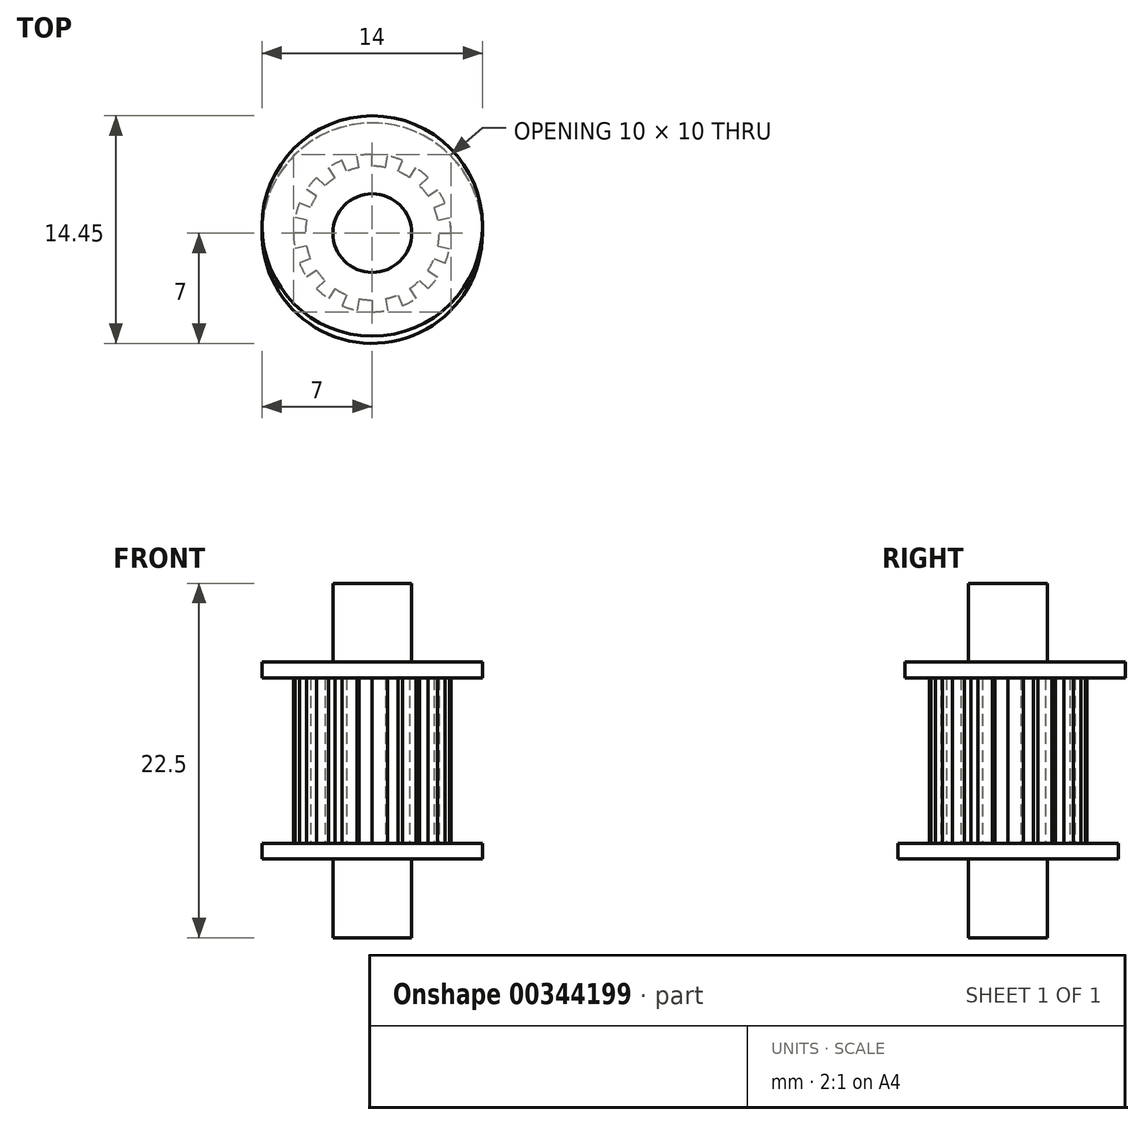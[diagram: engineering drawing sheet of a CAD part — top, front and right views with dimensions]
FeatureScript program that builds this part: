
annotation { "Feature Type Name" : "Feature", "Feature Type Description" : "" }
export const myFeature = defineFeature(function(context is Context, id is Id, definition is map)
    precondition{}
    {
        {
            var Q0;
            Q0=qCreatedBy(makeId("Top.planeOp"),FACE);
            var sketch = newSketch(context, id + "F0", { "sketchPlane" : qUnion([Q0])});
            skCircle(sketch, "E0", {"center": v(0, 0) * mm, "radius": 7 * mm});
            skSolve(sketch);
        }
        {
            var Q0;
            Q0=qSketchRegion(id+"F0",true);
            extrude(context, id + "F1", {"entities" : qUnion([Q0]), "depth" : 1 * mm});
        }
        {
            var Q0;
            Q0=makeQuery(id+"F1.opExtrude","CAP_FACE",FACE,{"disambiguationData":[OSD([sQuery(id+"F0.wireOp",EDGE,"E0")])],"isStart":false});
            var sketch = newSketch(context, id + "F2", { "sketchPlane" : qUnion([Q0])});
            skLineSegment(sketch, "E1", {"start": v(0, 4.25) * mm, "end": v(0, 5) * mm});
            skLineSegment(sketch, "E2.1.0", {"start": v(-0.83, 4.17) * mm, "end": v(-0.98, 4.9) * mm});
            skLineSegment(sketch, "E2.2.0", {"start": v(-1.63, 3.93) * mm, "end": v(-1.91, 4.62) * mm});
            skLineSegment(sketch, "E2.3.0", {"start": v(-2.36, 3.53) * mm, "end": v(-2.78, 4.16) * mm});
            skLineSegment(sketch, "E2.4.0", {"start": v(-3, 3) * mm, "end": v(-3.54, 3.54) * mm});
            skLineSegment(sketch, "E2.5.0", {"start": v(-3.53, 2.36) * mm, "end": v(-4.16, 2.78) * mm});
            skLineSegment(sketch, "E2.6.0", {"start": v(-3.93, 1.63) * mm, "end": v(-4.62, 1.91) * mm});
            skLineSegment(sketch, "E2.7.0", {"start": v(-4.17, 0.83) * mm, "end": v(-4.9, 0.98) * mm});
            skLineSegment(sketch, "E2.8.0", {"start": v(-4.25, 0) * mm, "end": v(-5, 0) * mm});
            skLineSegment(sketch, "E2.9.0", {"start": v(-4.17, -0.83) * mm, "end": v(-4.9, -0.98) * mm});
            skLineSegment(sketch, "E2.10.0", {"start": v(-3.93, -1.63) * mm, "end": v(-4.62, -1.91) * mm});
            skLineSegment(sketch, "E2.11.0", {"start": v(-3.53, -2.36) * mm, "end": v(-4.16, -2.78) * mm});
            skLineSegment(sketch, "E2.12.0", {"start": v(-3, -3) * mm, "end": v(-3.54, -3.54) * mm});
            skLineSegment(sketch, "E2.13.0", {"start": v(-2.36, -3.53) * mm, "end": v(-2.78, -4.16) * mm});
            skLineSegment(sketch, "E2.14.0", {"start": v(-1.63, -3.93) * mm, "end": v(-1.91, -4.62) * mm});
            skLineSegment(sketch, "E2.15.0", {"start": v(-0.83, -4.17) * mm, "end": v(-0.98, -4.9) * mm});
            skLineSegment(sketch, "E2.16.0", {"start": v(0, -4.25) * mm, "end": v(0, -5) * mm});
            skLineSegment(sketch, "E2.17.0", {"start": v(0.83, -4.17) * mm, "end": v(0.98, -4.9) * mm});
            skLineSegment(sketch, "E2.18.0", {"start": v(1.63, -3.93) * mm, "end": v(1.91, -4.62) * mm});
            skLineSegment(sketch, "E2.19.0", {"start": v(2.36, -3.53) * mm, "end": v(2.78, -4.16) * mm});
            skLineSegment(sketch, "E2.20.0", {"start": v(3, -3) * mm, "end": v(3.54, -3.54) * mm});
            skLineSegment(sketch, "E2.21.0", {"start": v(3.53, -2.36) * mm, "end": v(4.16, -2.78) * mm});
            skLineSegment(sketch, "E2.22.0", {"start": v(3.93, -1.63) * mm, "end": v(4.62, -1.91) * mm});
            skLineSegment(sketch, "E2.23.0", {"start": v(4.17, -0.83) * mm, "end": v(4.9, -0.98) * mm});
            skLineSegment(sketch, "E2.24.0", {"start": v(4.25, 0) * mm, "end": v(5, 0) * mm});
            skLineSegment(sketch, "E2.25.0", {"start": v(4.17, 0.83) * mm, "end": v(4.9, 0.98) * mm});
            skLineSegment(sketch, "E2.26.0", {"start": v(3.93, 1.63) * mm, "end": v(4.62, 1.91) * mm});
            skLineSegment(sketch, "E2.27.0", {"start": v(3.53, 2.36) * mm, "end": v(4.16, 2.78) * mm});
            skLineSegment(sketch, "E2.28.0", {"start": v(3, 3) * mm, "end": v(3.54, 3.54) * mm});
            skLineSegment(sketch, "E2.29.0", {"start": v(2.36, 3.53) * mm, "end": v(2.78, 4.16) * mm});
            skLineSegment(sketch, "E2.30.0", {"start": v(1.63, 3.93) * mm, "end": v(1.91, 4.62) * mm});
            skLineSegment(sketch, "E2.31.0", {"start": v(0.83, 4.17) * mm, "end": v(0.98, 4.9) * mm});
            skPoint(sketch, "E2.center", {"position": v(0, 0) * mm});
            skArc(sketch, "E3", {"start": v(-0.83, 4.17) * mm, "mid": v(-1.23, 4.07) * mm, "end": v(-1.63, 3.93) * mm});
            skArc(sketch, "E4", {"start": v(-1.91, 4.62) * mm, "mid": v(-2.36, 4.4) * mm, "end": v(-2.78, 4.16) * mm});
            skPoint(sketch, "E5.orphan", {"position": v(-1.14, 5.75) * mm});
            skArc(sketch, "E6.trimOffspring", {"start": v(0, 5) * mm, "mid": v(-0.5, 4.98) * mm, "end": v(-0.98, 4.9) * mm});
            skArc(sketch, "E7.trimOffspring", {"start": v(0.83, 4.17) * mm, "mid": v(0.42, 4.23) * mm, "end": v(0, 4.25) * mm});
            skArc(sketch, "E8.trimOffspring", {"start": v(1.91, 4.62) * mm, "mid": v(1.45, 4.78) * mm, "end": v(0.98, 4.9) * mm});
            skArc(sketch, "E9.trimOffspring", {"start": v(2.36, 3.53) * mm, "mid": v(2, 3.75) * mm, "end": v(1.63, 3.93) * mm});
            skArc(sketch, "E10.trimOffspring", {"start": v(3.54, 3.54) * mm, "mid": v(3.17, 3.87) * mm, "end": v(2.78, 4.16) * mm});
            skArc(sketch, "E11.trimOffspring", {"start": v(3.53, 2.36) * mm, "mid": v(3.29, 2.7) * mm, "end": v(3, 3) * mm});
            skArc(sketch, "E12.trimOffspring", {"start": v(4.62, 1.91) * mm, "mid": v(4.4, 2.36) * mm, "end": v(4.16, 2.78) * mm});
            skArc(sketch, "E13.trimOffspring", {"start": v(4.17, 0.83) * mm, "mid": v(4.07, 1.23) * mm, "end": v(3.93, 1.63) * mm});
            skArc(sketch, "E14.trimOffspring", {"start": v(5, 0) * mm, "mid": v(4.98, 0.5) * mm, "end": v(4.9, 0.98) * mm});
            skArc(sketch, "E15.trimOffspring", {"start": v(4.17, -0.83) * mm, "mid": v(4.23, -0.42) * mm, "end": v(4.25, 0) * mm});
            skArc(sketch, "E16.trimOffspring", {"start": v(4.62, -1.91) * mm, "mid": v(4.78, -1.45) * mm, "end": v(4.9, -0.98) * mm});
            skArc(sketch, "E17.trimOffspring", {"start": v(3.53, -2.36) * mm, "mid": v(3.75, -2) * mm, "end": v(3.93, -1.63) * mm});
            skArc(sketch, "E18.trimOffspring", {"start": v(3.54, -3.54) * mm, "mid": v(3.87, -3.17) * mm, "end": v(4.16, -2.78) * mm});
            skArc(sketch, "E19.trimOffspring", {"start": v(2.36, -3.53) * mm, "mid": v(2.7, -3.29) * mm, "end": v(3, -3) * mm});
            skArc(sketch, "E20.trimOffspring", {"start": v(1.91, -4.62) * mm, "mid": v(2.36, -4.4) * mm, "end": v(2.78, -4.16) * mm});
            skArc(sketch, "E21.trimOffspring", {"start": v(0.83, -4.17) * mm, "mid": v(1.23, -4.07) * mm, "end": v(1.63, -3.93) * mm});
            skArc(sketch, "E22.trimOffspring", {"start": v(0, -5) * mm, "mid": v(0.5, -4.98) * mm, "end": v(0.98, -4.9) * mm});
            skArc(sketch, "E23.trimOffspring", {"start": v(-0.83, -4.17) * mm, "mid": v(-0.42, -4.23) * mm, "end": v(0, -4.25) * mm});
            skArc(sketch, "E24.trimOffspring", {"start": v(-2.36, -3.53) * mm, "mid": v(-2, -3.75) * mm, "end": v(-1.63, -3.93) * mm});
            skArc(sketch, "E25.trimOffspring", {"start": v(-3.53, -2.36) * mm, "mid": v(-3.29, -2.7) * mm, "end": v(-3, -3) * mm});
            skArc(sketch, "E26.trimOffspring", {"start": v(-4.17, -0.83) * mm, "mid": v(-4.07, -1.23) * mm, "end": v(-3.93, -1.63) * mm});
            skArc(sketch, "E27.trimOffspring", {"start": v(-4.17, 0.83) * mm, "mid": v(-4.23, 0.42) * mm, "end": v(-4.25, 0) * mm});
            skArc(sketch, "E28.trimOffspring", {"start": v(-3.53, 2.36) * mm, "mid": v(-3.75, 2) * mm, "end": v(-3.93, 1.63) * mm});
            skArc(sketch, "E29.trimOffspring", {"start": v(-2.36, 3.53) * mm, "mid": v(-2.7, 3.29) * mm, "end": v(-3, 3) * mm});
            skArc(sketch, "E30.trimOffspring", {"start": v(-3.54, 3.54) * mm, "mid": v(-3.87, 3.17) * mm, "end": v(-4.16, 2.78) * mm});
            skArc(sketch, "E31.trimOffspring", {"start": v(-4.62, 1.91) * mm, "mid": v(-4.78, 1.45) * mm, "end": v(-4.9, 0.98) * mm});
            skArc(sketch, "E32.trimOffspring", {"start": v(-5, 0) * mm, "mid": v(-4.98, -0.5) * mm, "end": v(-4.9, -0.98) * mm});
            skArc(sketch, "E33.trimOffspring", {"start": v(-4.62, -1.91) * mm, "mid": v(-4.4, -2.36) * mm, "end": v(-4.16, -2.78) * mm});
            skArc(sketch, "E34.trimOffspring", {"start": v(-3.54, -3.54) * mm, "mid": v(-3.17, -3.87) * mm, "end": v(-2.78, -4.16) * mm});
            skArc(sketch, "E35.trimOffspring", {"start": v(-1.91, -4.62) * mm, "mid": v(-1.45, -4.78) * mm, "end": v(-0.98, -4.9) * mm});
            skPoint(sketch, "E36.orphan", {"position": v(1.14, 5.75) * mm});
            skPoint(sketch, "E37.orphan", {"position": v(0, 5.86) * mm});
            skPoint(sketch, "E38.orphan", {"position": v(2.24, 5.41) * mm});
            skPoint(sketch, "E39.orphan", {"position": v(3.25, 4.87) * mm});
            skPoint(sketch, "E40.orphan", {"position": v(4.14, 4.14) * mm});
            skPoint(sketch, "E41.orphan", {"position": v(4.87, 3.25) * mm});
            skPoint(sketch, "E42.orphan", {"position": v(5.41, 2.24) * mm});
            skPoint(sketch, "E43.orphan", {"position": v(5.75, 1.14) * mm});
            skPoint(sketch, "E44.orphan", {"position": v(5.86, 0) * mm});
            skPoint(sketch, "E45.orphan", {"position": v(5.75, -1.14) * mm});
            skPoint(sketch, "E46.orphan", {"position": v(5.41, -2.24) * mm});
            skPoint(sketch, "E47.orphan", {"position": v(4.87, -3.25) * mm});
            skPoint(sketch, "E48.orphan", {"position": v(4.14, -4.14) * mm});
            skPoint(sketch, "E49.orphan", {"position": v(3.25, -4.87) * mm});
            skPoint(sketch, "E50.orphan", {"position": v(2.24, -5.41) * mm});
            skPoint(sketch, "E51.orphan", {"position": v(1.14, -5.75) * mm});
            skPoint(sketch, "E52.orphan", {"position": v(0, -5.86) * mm});
            skPoint(sketch, "E53.orphan", {"position": v(-1.14, -5.75) * mm});
            skPoint(sketch, "E54.orphan", {"position": v(-2.24, -5.41) * mm});
            skPoint(sketch, "E55.orphan", {"position": v(-3.25, -4.87) * mm});
            skPoint(sketch, "E56.orphan", {"position": v(-4.14, -4.14) * mm});
            skPoint(sketch, "E57.orphan", {"position": v(-4.87, -3.25) * mm});
            skPoint(sketch, "E58.orphan", {"position": v(-5.41, -2.24) * mm});
            skPoint(sketch, "E59.orphan", {"position": v(-5.75, -1.14) * mm});
            skPoint(sketch, "E60.orphan", {"position": v(-5.86, 0) * mm});
            skPoint(sketch, "E61.orphan", {"position": v(-5.75, 1.14) * mm});
            skPoint(sketch, "E62.orphan", {"position": v(-5.41, 2.24) * mm});
            skPoint(sketch, "E63.orphan", {"position": v(-4.87, 3.25) * mm});
            skPoint(sketch, "E64.orphan", {"position": v(-4.14, 4.14) * mm});
            skPoint(sketch, "E65.orphan", {"position": v(-3.25, 4.87) * mm});
            skPoint(sketch, "E66.orphan", {"position": v(-2.24, 5.41) * mm});
            skSolve(sketch);
        }
        {
            var Q0;
            Q0=qSketchRegion(id+"F2",true);
            extrude(context, id + "F3", {"entities" : qUnion([Q0]), "operationType" : NewBodyOperationType.ADD, "depth" : 10.5 * mm});
        }
        {
            var Q0;
            Q0=makeQuery(id+"F3.opExtrude","CAP_FACE",FACE,{"disambiguationData":[OSD([sQuery(id+"F2.wireOp",EDGE,"E1"),sQuery(id+"F2.wireOp",EDGE,"E2.1.0"),sQuery(id+"F2.wireOp",EDGE,"E2.2.0"),sQuery(id+"F2.wireOp",EDGE,"E2.3.0"),sQuery(id+"F2.wireOp",EDGE,"E2.4.0"),sQuery(id+"F2.wireOp",EDGE,"E2.5.0"),sQuery(id+"F2.wireOp",EDGE,"E2.6.0"),sQuery(id+"F2.wireOp",EDGE,"E2.7.0"),sQuery(id+"F2.wireOp",EDGE,"E2.8.0"),sQuery(id+"F2.wireOp",EDGE,"E2.9.0"),sQuery(id+"F2.wireOp",EDGE,"E2.10.0"),sQuery(id+"F2.wireOp",EDGE,"E2.11.0"),sQuery(id+"F2.wireOp",EDGE,"E2.12.0"),sQuery(id+"F2.wireOp",EDGE,"E2.13.0"),sQuery(id+"F2.wireOp",EDGE,"E2.14.0"),sQuery(id+"F2.wireOp",EDGE,"E2.15.0"),sQuery(id+"F2.wireOp",EDGE,"E2.16.0"),sQuery(id+"F2.wireOp",EDGE,"E2.17.0"),sQuery(id+"F2.wireOp",EDGE,"E2.18.0"),sQuery(id+"F2.wireOp",EDGE,"E2.19.0"),sQuery(id+"F2.wireOp",EDGE,"E2.20.0"),sQuery(id+"F2.wireOp",EDGE,"E2.21.0"),sQuery(id+"F2.wireOp",EDGE,"E2.22.0"),sQuery(id+"F2.wireOp",EDGE,"E2.23.0"),sQuery(id+"F2.wireOp",EDGE,"E2.24.0"),sQuery(id+"F2.wireOp",EDGE,"E2.25.0"),sQuery(id+"F2.wireOp",EDGE,"E2.26.0"),sQuery(id+"F2.wireOp",EDGE,"E2.27.0"),sQuery(id+"F2.wireOp",EDGE,"E2.28.0"),sQuery(id+"F2.wireOp",EDGE,"E2.29.0"),sQuery(id+"F2.wireOp",EDGE,"E2.30.0"),sQuery(id+"F2.wireOp",EDGE,"E2.31.0"),sQuery(id+"F2.wireOp",EDGE,"E3"),sQuery(id+"F2.wireOp",EDGE,"E4"),sQuery(id+"F2.wireOp",EDGE,"E6.trimOffspring"),sQuery(id+"F2.wireOp",EDGE,"E7.trimOffspring"),sQuery(id+"F2.wireOp",EDGE,"E8.trimOffspring"),sQuery(id+"F2.wireOp",EDGE,"E9.trimOffspring"),sQuery(id+"F2.wireOp",EDGE,"E10.trimOffspring"),sQuery(id+"F2.wireOp",EDGE,"E11.trimOffspring"),sQuery(id+"F2.wireOp",EDGE,"E12.trimOffspring"),sQuery(id+"F2.wireOp",EDGE,"E13.trimOffspring"),sQuery(id+"F2.wireOp",EDGE,"E14.trimOffspring"),sQuery(id+"F2.wireOp",EDGE,"E15.trimOffspring"),sQuery(id+"F2.wireOp",EDGE,"E16.trimOffspring"),sQuery(id+"F2.wireOp",EDGE,"E17.trimOffspring"),sQuery(id+"F2.wireOp",EDGE,"E18.trimOffspring"),sQuery(id+"F2.wireOp",EDGE,"E19.trimOffspring"),sQuery(id+"F2.wireOp",EDGE,"E20.trimOffspring"),sQuery(id+"F2.wireOp",EDGE,"E21.trimOffspring"),sQuery(id+"F2.wireOp",EDGE,"E22.trimOffspring"),sQuery(id+"F2.wireOp",EDGE,"E23.trimOffspring"),sQuery(id+"F2.wireOp",EDGE,"E24.trimOffspring"),sQuery(id+"F2.wireOp",EDGE,"E25.trimOffspring"),sQuery(id+"F2.wireOp",EDGE,"E26.trimOffspring"),sQuery(id+"F2.wireOp",EDGE,"E27.trimOffspring"),sQuery(id+"F2.wireOp",EDGE,"E28.trimOffspring"),sQuery(id+"F2.wireOp",EDGE,"E29.trimOffspring"),sQuery(id+"F2.wireOp",EDGE,"E30.trimOffspring"),sQuery(id+"F2.wireOp",EDGE,"E31.trimOffspring"),sQuery(id+"F2.wireOp",EDGE,"E32.trimOffspring"),sQuery(id+"F2.wireOp",EDGE,"E33.trimOffspring"),sQuery(id+"F2.wireOp",EDGE,"E34.trimOffspring"),sQuery(id+"F2.wireOp",EDGE,"E35.trimOffspring")])],"isStart":false});
            var sketch = newSketch(context, id + "F4", { "sketchPlane" : qUnion([Q0])});
            skCircle(sketch, "E67", {"center": v(0, 0.45) * mm, "radius": 7 * mm});
            skSolve(sketch);
        }
        {
            var Q0;
            Q0=qSketchRegion(id+"F4",true);
            extrude(context, id + "F5", {"entities" : qUnion([Q0]), "operationType" : NewBodyOperationType.ADD, "depth" : 1 * mm});
        }
        {
            var Q0;
            Q0=makeQuery(id+"F1.opExtrude","CAP_FACE",FACE,{"disambiguationData":[OSD([sQuery(id+"F0.wireOp",EDGE,"E0")])],"isStart":true});
            var sketch = newSketch(context, id + "F6", { "sketchPlane" : qUnion([Q0])});
            skCircle(sketch, "E68", {"center": v(0, 0) * mm, "radius": 2.5 * mm});
            skSolve(sketch);
        }
        {
            var Q0;
            Q0 = qSketchRegion(id + "F6", true);
            extrude(context, id + "F7", {"entities" : qUnion([Q0]), "operationType" : NewBodyOperationType.ADD, "depth" : 5 * mm, "hasSecondDirection" : true, "secondDirectionOppositeDirection" : true, "secondDirectionDepth" : 17.5 * mm});
        }
    });
